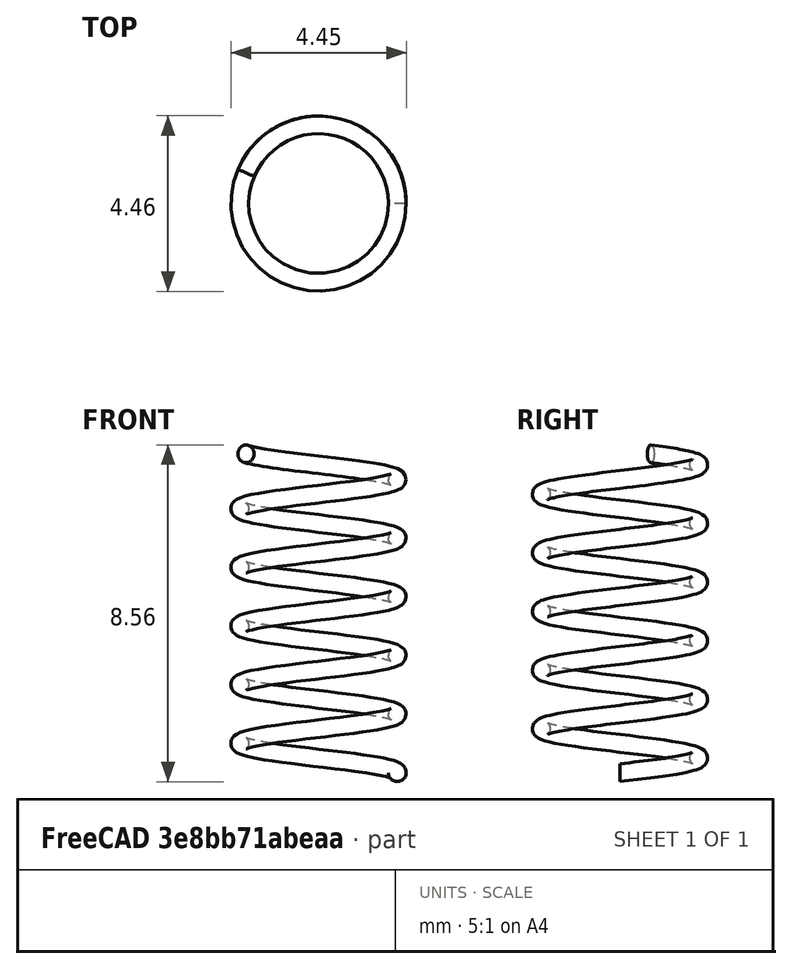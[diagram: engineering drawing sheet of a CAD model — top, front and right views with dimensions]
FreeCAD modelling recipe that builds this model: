
FCSTD DOCUMENT  (FreeCAD 1.0R39109 (Git))
Label: 1
License: All rights reserved
LicenseURL: https://en.wikipedia.org/wiki/All_rights_reserved
objects: Sketcher::SketchObject×1, PartDesign::AdditiveHelix×1, PartDesign::Body×1
note: 6 computed .brp shape members not serialized (recipe doc carries the construction recipe); baked Part::Feature solids carry a one-line shape summary decoded from their .brp

FEATURE [Sketcher::SketchObject] Sketch
  ArcFitTolerance = 1e-06
  AttachmentSupport = -> [XZ_Plane]
  FullyConstrained = true
  MakeInternals = false
  MapMode = 5
  Placement = pos=(0,0,0) rot=(1,0,0;1.5708rad)
  sketch-geometry (1):
    g0: Circle CenterX=2 CenterY=0 CenterZ=0 NormalX=0 NormalY=0 NormalZ=1 AngleXU=0 Radius=0.225
  constraints (3):
    c: Diameter(g0) = 0.45
    c: PointOnObject(g0,g-1)
    c: Distance(g0,g-2) = 2
FEATURE [PartDesign::AdditiveHelix] AdditiveHelix
  Angle = 0
  Axis = (1e-16,1e-16,1)
  Base = (0,0,0)
  Growth = 0
  HasBeenEdited = true
  Height = 8.1
  LeftHanded = false
  Mode = 0
  Outside = false
  Pitch = 1.49
  Placement = pos=(0,0,0) rot=(1,0,0;1.5708rad)
  Profile = -> Sketch
  ReferenceAxis = -> Z_Axis
  Refine = true
  Suppressed = false
  Tolerance = 0.1
  Turns = 5.43624
FEATURE [PartDesign::Body] Body
  AllowCompound = false
  Group = -> [Sketch,AdditiveHelix]
  Origin = -> Origin
  Tip = -> AdditiveHelix
